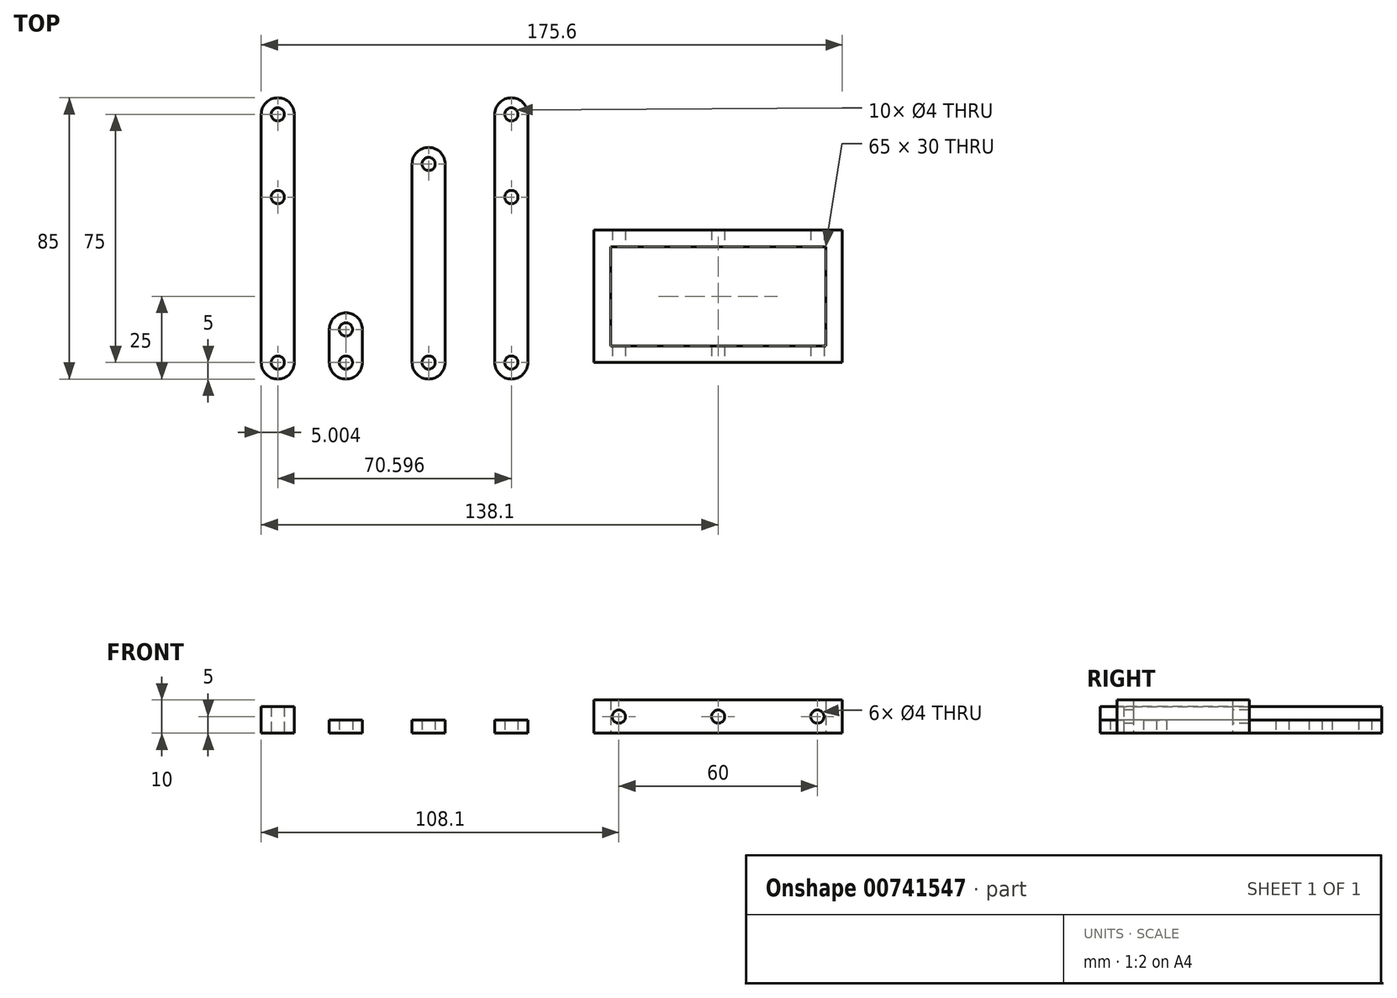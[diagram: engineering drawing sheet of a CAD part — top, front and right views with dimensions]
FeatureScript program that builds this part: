
annotation { "Feature Type Name" : "Feature", "Feature Type Description" : "" }
export const myFeature = defineFeature(function(context is Context, id is Id, definition is map)
    precondition{}
    {
        {
            var Q0;
            Q0=qCreatedBy(makeId("Top.planeOp"),FACE);
            var sketch = newSketch(context, id + "F0", { "sketchPlane" : qUnion([Q0])});
            skLineSegment(sketch, "E0.bottom", {"start": v(0, 0) * mm, "end": v(75, 0) * mm});
            skLineSegment(sketch, "E0.top", {"start": v(0, 40) * mm, "end": v(75, 40) * mm});
            skLineSegment(sketch, "E0.left", {"start": v(0, 0) * mm, "end": v(0, 40) * mm});
            skLineSegment(sketch, "E0.right", {"start": v(75, 0) * mm, "end": v(75, 40) * mm});
            skLineSegment(sketch, "E1.0", {"start": v(5, 35) * mm, "end": v(70, 35) * mm});
            skLineSegment(sketch, "E2.0", {"start": v(5, 5) * mm, "end": v(5, 35) * mm});
            skLineSegment(sketch, "E3.0", {"start": v(5, 5) * mm, "end": v(70, 5) * mm});
            skLineSegment(sketch, "E4.0", {"start": v(70, 5) * mm, "end": v(70, 35) * mm});
            skSolve(sketch);
        }
        {
            var Q0;
            Q0=makeQuery(id+"F0.imprint","IMPRINT",FACE,{"disambiguationData":[TD([[makeQuery(id+"F0.imprint","IMPRINT",EDGE,{"derivedFrom":sQuery(id+"F0.wireOp",EDGE,"E0.bottom")}),1.0]])]});
            extrude(context, id + "F1", {"entities" : qUnion([Q0]), "depth" : 10 * mm, "offsetDistance" : 25 * mm});
        }
        {
            var Q0;
            Q0=qCreatedBy(makeId("Front.planeOp"),FACE);
            var sketch = newSketch(context, id + "F2", { "sketchPlane" : qUnion([Q0])});
            skCircle(sketch, "E5", {"center": v(7.5, 5) * mm, "radius": 2 * mm});
            skCircle(sketch, "E6", {"center": v(37.5, 5) * mm, "radius": 2 * mm});
            skCircle(sketch, "E7", {"center": v(67.5, 5) * mm, "radius": 2 * mm});
            skSolve(sketch);
        }
        {
            var Q0;
            Q0 = qSketchRegion(id + "F2", true);
            extrude(context, id + "F3", {"entities" : qUnion([Q0]), "operationType" : NewBodyOperationType.REMOVE, "endBound" : BoundingType.THROUGH_ALL, "oppositeDirection" : true, "depth" : 25 * mm, "offsetDistance" : 25 * mm});
        }
        {
            var Q0;
            Q0=qCreatedBy(makeId("Top.planeOp"),FACE);
            var sketch = newSketch(context, id + "F4", { "sketchPlane" : qUnion([Q0])});
            skCircle(sketch, "E8", {"center": v(-75, 0) * mm, "radius": 2 * mm});
            skCircle(sketch, "E9", {"center": v(-75, 10) * mm, "radius": 2 * mm});
            skCircle(sketch, "E10", {"center": v(-50, 60) * mm, "radius": 2 * mm});
            skCircle(sketch, "E11", {"center": v(-50, 0) * mm, "radius": 2 * mm});
            skCircle(sketch, "E12", {"center": v(-25, 75) * mm, "radius": 2 * mm});
            skCircle(sketch, "E13", {"center": v(-25, 0) * mm, "radius": 2 * mm});
            skArc(sketch, "E14", {"start": v(-70, 10) * mm, "mid": v(-75, 15) * mm, "end": v(-80, 10) * mm});
            skArc(sketch, "E15", {"start": v(-80, 0) * mm, "mid": v(-75, -5) * mm, "end": v(-70, 0) * mm});
            skArc(sketch, "E16", {"start": v(-45, 60) * mm, "mid": v(-50, 65) * mm, "end": v(-55, 60) * mm});
            skArc(sketch, "E17", {"start": v(-55, 0) * mm, "mid": v(-50, -5) * mm, "end": v(-45, 0) * mm});
            skArc(sketch, "E18", {"start": v(-20, 75) * mm, "mid": v(-25, 80) * mm, "end": v(-30, 75) * mm});
            skArc(sketch, "E19", {"start": v(-30, 0) * mm, "mid": v(-25, -5) * mm, "end": v(-20, 0) * mm});
            skCircle(sketch, "E20", {"center": v(-25, 50) * mm, "radius": 2 * mm});
            skLineSegment(sketch, "E21", {"start": v(-20, 75) * mm, "end": v(-20, 0) * mm});
            skLineSegment(sketch, "E22", {"start": v(-30, 75) * mm, "end": v(-30, 0) * mm});
            skLineSegment(sketch, "E23", {"start": v(-70, 10) * mm, "end": v(-70, 0) * mm});
            skLineSegment(sketch, "E24", {"start": v(-80, 10) * mm, "end": v(-80, 0) * mm});
            skLineSegment(sketch, "E25", {"start": v(-45, 60) * mm, "end": v(-45, 0) * mm});
            skLineSegment(sketch, "E26", {"start": v(-55, 60) * mm, "end": v(-55, 0) * mm});
            skSolve(sketch);
        }
        {
            var Q0;
            Q0=makeQuery(id+"F4.imprint","IMPRINT",FACE,{"disambiguationData":[TD([[makeQuery(id+"F4.imprint","IMPRINT",EDGE,{"derivedFrom":sQuery(id+"F4.wireOp",EDGE,"E8")}),-1.0]])]});
            var Q1;
            Q1=makeQuery(id+"F4.imprint","IMPRINT",FACE,{"disambiguationData":[TD([[makeQuery(id+"F4.imprint","IMPRINT",EDGE,{"derivedFrom":sQuery(id+"F4.wireOp",EDGE,"E10")}),-1.0]])]});
            var Q2;
            Q2=makeQuery(id+"F4.imprint","IMPRINT",FACE,{"disambiguationData":[TD([[makeQuery(id+"F4.imprint","IMPRINT",EDGE,{"derivedFrom":sQuery(id+"F4.wireOp",EDGE,"E12")}),-1.0]])]});
            extrude(context, id + "F5", {"entities" : qUnion([Q0, Q1, Q2]), "depth" : 4 * mm, "offsetDistance" : 25 * mm});
        }
        {
            var Q0;
            Q0=qCreatedBy(makeId("Top.planeOp"),FACE);
            var sketch = newSketch(context, id + "F6", { "sketchPlane" : qUnion([Q0])});
            skArc(sketch, "E27", {"start": v(-100.6, 0) * mm, "mid": v(-95.6, -5) * mm, "end": v(-90.6, 0) * mm});
            skCircle(sketch, "E28", {"center": v(-95.6, 0) * mm, "radius": 2 * mm});
            skArc(sketch, "E29", {"start": v(-90.6, 75) * mm, "mid": v(-95.6, 80) * mm, "end": v(-100.6, 75) * mm});
            skCircle(sketch, "E30", {"center": v(-95.6, 75) * mm, "radius": 2 * mm});
            skLineSegment(sketch, "E31", {"start": v(-100.6, 75) * mm, "end": v(-100.6, 0) * mm});
            skLineSegment(sketch, "E32", {"start": v(-90.6, 0) * mm, "end": v(-90.6, 75) * mm});
            skCircle(sketch, "E33", {"center": v(-95.6, 50) * mm, "radius": 2 * mm});
            skSolve(sketch);
        }
        {
            var Q0;
            Q0 = qSketchRegion(id + "F6", true);
            extrude(context, id + "F7", {"entities" : qUnion([Q0]), "depth" : 8 * mm, "offsetDistance" : 25 * mm});
        }
    });
